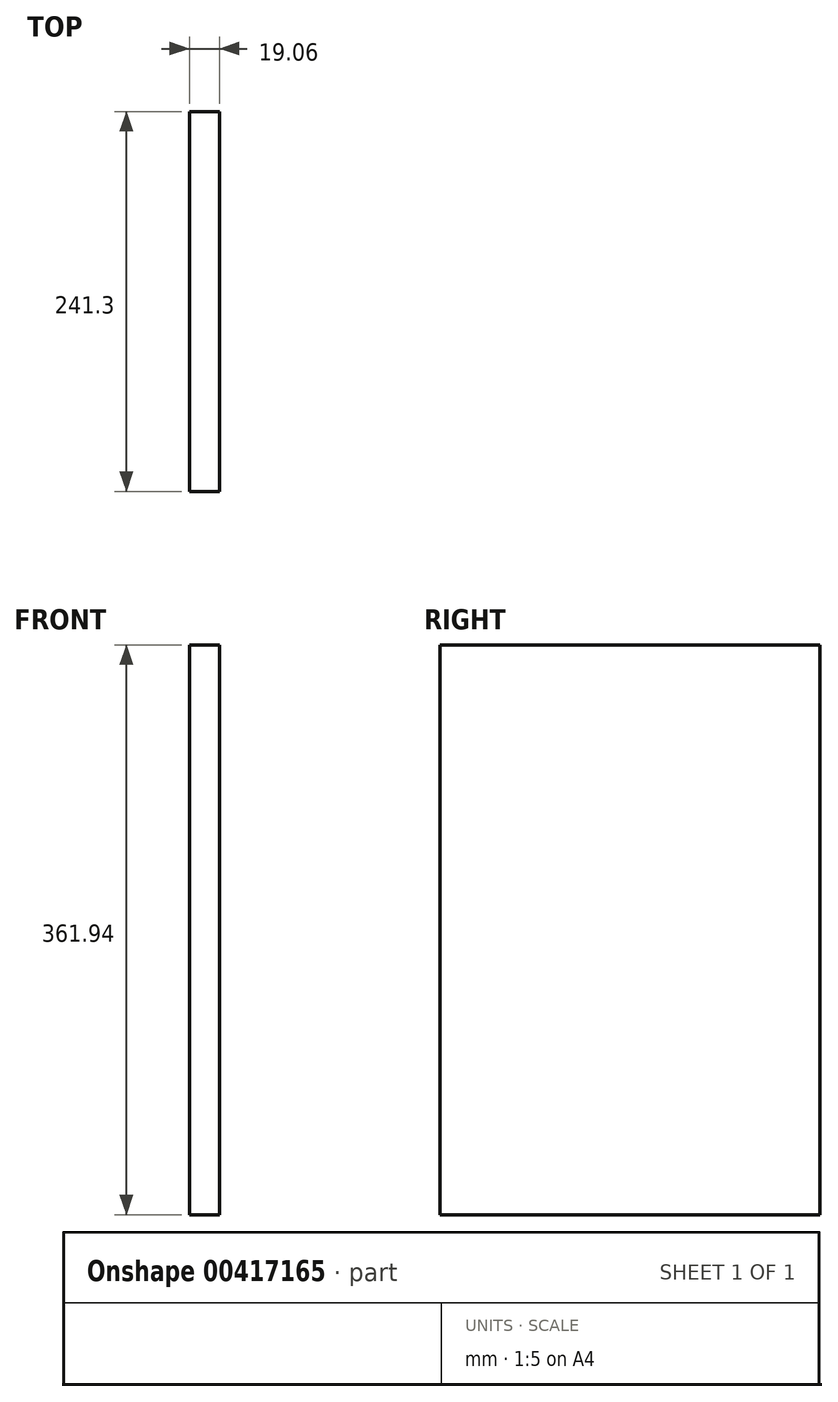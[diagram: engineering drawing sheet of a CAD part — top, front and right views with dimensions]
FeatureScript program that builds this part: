
annotation { "Feature Type Name" : "Feature", "Feature Type Description" : "" }
export const myFeature = defineFeature(function(context is Context, id is Id, definition is map)
    precondition{}
    {
        {
            var Q0;
            Q0=qCreatedBy(makeId("Front.planeOp"),FACE);
            var sketch = newSketch(context, id + "F0", { "sketchPlane" : qUnion([Q0])});
            skLineSegment(sketch, "E0.bottom", {"start": v(9.52, -180.98) * mm, "end": v(-9.53, -180.98) * mm});
            skLineSegment(sketch, "E0.top", {"start": v(9.53, 180.98) * mm, "end": v(-9.52, 180.98) * mm});
            skLineSegment(sketch, "E0.left", {"start": v(9.52, -180.98) * mm, "end": v(9.53, 180.98) * mm});
            skLineSegment(sketch, "E0.right", {"start": v(-9.53, -180.98) * mm, "end": v(-9.52, 180.98) * mm});
            skPoint(sketch, "E0.middle", {"position": v(0, 0) * mm});
            skSolve(sketch);
        }
        {
            var Q0;
            Q0 = qSketchRegion(id + "F0", true);
            extrude(context, id + "F1", {"entities" : qUnion([Q0]), "depth" : 241.3 * mm});
        }
    });
